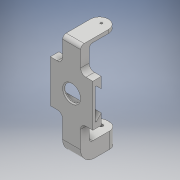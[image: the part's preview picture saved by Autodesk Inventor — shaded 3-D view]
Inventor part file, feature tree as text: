
AUTODESK INVENTOR PART (.ipt)
format: ipt  version: 2017 (Build 210142000, 142)  size: 243,200 bytes
history: native  units: mm
features: fillet x8, extrude x7, sketch x6, hole x2
ambient origin geometry x8: Origin, YZ Plane, XZ Plane, XY Plane, X Axis, Y Axis, Z Axis, Center Point
bodies: Solid1 (feature_tree)
feature tree (23):
  extrude  "Block"  Depth=12.0mm
  extrude  "Tripod Slot"  Depth=60.0mm
  hole  "Hole1"  [1 undecoded]
  extrude  "Extrusion4"  Depth=21.75mm
  extrude  "Extrusion5"  Depth=2.0mm
  extrude  "Extrusion6"  Depth=30.0mm
  fillet  "Fillet4"  Radius=52.5mm
  fillet  "Fillet5"  Radius=40.0mm
  fillet  "Fillet6"  Radius=5.0mm
  extrude  "Extrusion7"  Depth=10.0mm
  extrude  "Extrusion8"  Depth=1.5mm TaperAngle=0.0deg
  hole  "Hole2"  [1 undecoded]
  fillet  "Fillet7"  Radius=4.413583mm
  fillet  "Fillet8"  Radius=17.3mm
  fillet  "Fillet9"  Radius=22.5mm
  fillet  "Fillet10"  Radius=3.0mm
  fillet  "Fillet11"  Radius=11.0mm
  sketch  "Sketch2"  dims[d0=60.0mm d1=12.0mm]
  sketch  "Sketch4"  dims[d14=60.0mm d15=0.0mm d17=14.75mm]
  sketch  "Sketch5"  dims[d18=14.75mm d19=8.9mm]
  sketch  "Sketch6"  dims[d20=21.75mm d21=21.75mm]
  sketch  "Sketch7"  dims[d22=2.0mm d23=2.0mm]
  sketch  "Sketch8"  dims[d24=60.0mm d25=0.0mm d46=30.0mm d47=30.0mm d48=22.5mm d49=6.0mm d50=4.0mm d51=2.0mm d52=90.0deg d53=8.0mm d54=20.594885mm d55=52.5mm d56=0.0mm d58=40.0mm d59=0.0mm d60=5.0mm d61=10.0mm d62=31.75mm d63=0.0mm d64=25.4mm d65=4.413583mm d66=17.3mm d67=22.5mm d68=3.0mm d70=11.0mm d71=20.0mm d72=5.0mm d73=25.4mm d74=35.0mm d75=0.0mm d76=2.5mm d79=40.0mm d80=0.0mm d81=5.0mm d82=10.0mm d83=12.7mm d84=3.0mm d85=6.0mm d86=4.0mm d87=2.0mm d88=90.0deg d89=8.0mm d90=20.594885mm d91=12.7mm d92=5.0mm d93=5.0mm d94=7.5mm d95=1.5mm]
note: 2 required parameter values undecoded (feature->parameter linkage not recoverable at this tier; creation-order binding heuristic only, values carry confidence <= 0.55)
